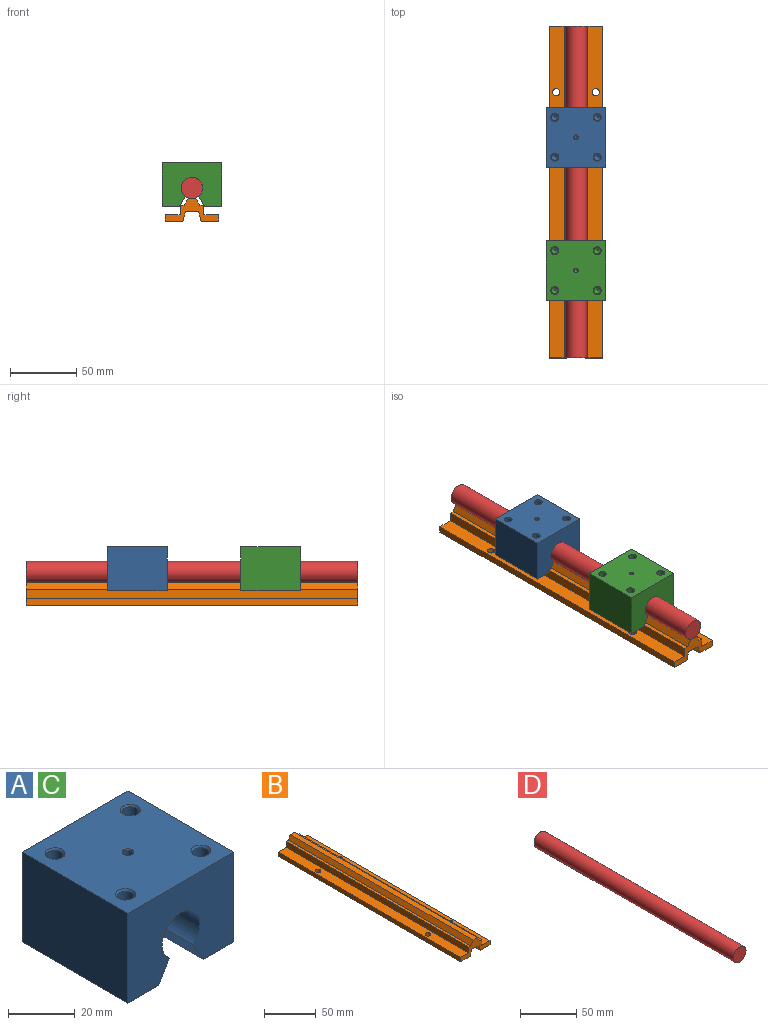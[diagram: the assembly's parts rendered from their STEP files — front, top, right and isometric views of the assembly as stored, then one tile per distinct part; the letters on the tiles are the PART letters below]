
ASSEMBLY  parts=4 mates=2
PART A: 25 faces, bbox 45x45x33 mm
  f0: plane 45x7.77mm, normal (0.87,0,-0.5), area 403.6mm2, adj f1,f7,f8,f9
  f1: cylinder r=8mm len=45mm, axis (0,1,0), area 1774.1mm2, adj f0,f2,f8,f9
  f2: plane 45x7.77mm, normal (-0.87,0,-0.5), area 403.6mm2, adj f1,f3,f8,f9
  f3: plane 45x13mm, normal (0,0,-1), area 585mm2, adj f2,f4,f8,f9
  f4: plane 45x33mm, normal (1,0,0), area 1485mm2, adj f3,f5,f8,f9
  f5: plane 45x45mm, normal (0,0,1), area 1902.3mm2, adj f4,f6,f8,f9,f12,f15,f18,f21
  f6: plane 45x33mm, normal (-1,0,0), area 1485mm2, adj f5,f7,f8,f9
  f7: plane 45x13mm, normal (0,0,-1), area 585mm2, adj f0,f6,f8,f9
  f8: plane 45x33mm, normal (0,-1,0), area 1183.3mm2, adj f0,f1,f2,f3,f4,f5,f6,f7
  f9: plane 45x33mm, normal (0,1,0), area 1183.3mm2, adj f0,f1,f2,f3,f4,f5,f6,f7
  f10: cone r=0mm half-angle=59deg, axis (0,0,1), area 22.9mm2, adj f11
  f11: cylinder r=2.5mm len=11.4mm, axis (0,0,1), area 179.1mm2, adj f10,f12
  f12: cone r=2.5mm half-angle=40deg, axis (0,0,1), area 13.4mm2, adj f5,f11
  f13: cone r=0mm half-angle=59deg, axis (0,0,1), area 22.9mm2, adj f14
  f14: cylinder r=2.5mm len=11.4mm, axis (0,0,1), area 179.1mm2, adj f13,f15
  f15: cone r=2.5mm half-angle=40deg, axis (0,0,1), area 13.4mm2, adj f5,f14
  f16: cone r=0mm half-angle=59deg, axis (0,0,1), area 22.9mm2, adj f17
  f17: cylinder r=2.5mm len=11.4mm, axis (0,0,1), area 179.1mm2, adj f16,f18
  f18: cone r=2.5mm half-angle=40deg, axis (0,0,1), area 13.4mm2, adj f5,f17
  f19: cone r=0mm half-angle=59deg, axis (0,0,1), area 22.9mm2, adj f20
  f20: cylinder r=2.5mm len=11.4mm, axis (0,0,1), area 179.1mm2, adj f19,f21
  f21: cone r=2.5mm half-angle=40deg, axis (0,0,1), area 13.4mm2, adj f5,f20
  f22: cone r=0mm half-angle=59deg, axis (0,0,1), area 8.2mm2, adj f23
  f23: cylinder r=1.5mm len=4.7mm, axis (0,0,1), area 44.3mm2, adj f22,f24
  f24: cone r=1.5mm half-angle=40deg, axis (0,0,1), area 4mm2, adj f5,f23
PART B: 22 faces, bbox 40x250x17 mm
  f0: plane 250x5mm, normal (-1,0,0), area 1250mm2, adj f1,f15,f16,f17
  f1: plane 250x13mm, normal (0,0,-1), area 3202.5mm2, adj f0,f2,f16,f17,f18,f19
  f2: plane 250x7.01mm, normal (0.96,0,-0.27), area 1822.5mm2, adj f1,f3,f16,f17
  f3: plane 250x10mm, normal (0,0,-1), area 2500mm2, adj f2,f4,f16,f17
  f4: plane 250x7.01mm, normal (-0.96,0,-0.27), area 1822.5mm2, adj f3,f5,f16,f17
  f5: plane 250x13mm, normal (0,0,-1), area 3202.5mm2, adj f4,f6,f16,f17,f20,f21
  f6: plane 250x5mm, normal (1,0,0), area 1250mm2, adj f5,f7,f16,f17
  f7: plane 250x11mm, normal (0,0,1), area 2702.5mm2, adj f6,f8,f16,f17,f20,f21
  f8: plane 250x7mm, normal (1,0,0), area 1750mm2, adj f7,f9,f16,f17
  f9: plane 250x3mm, normal (0,0,1), area 750mm2, adj f8,f10,f16,f17
  f10: plane 250x5mm, normal (0.86,0,0.51), area 1457.7mm2, adj f9,f11,f16,f17
  f11: plane 250x6mm, normal (0,0,1), area 1500mm2, adj f10,f12,f16,f17
  f12: plane 250x5mm, normal (-0.86,0,0.51), area 1457.7mm2, adj f11,f13,f16,f17
  f13: plane 250x3mm, normal (0,0,1), area 750mm2, adj f12,f14,f16,f17
  f14: plane 250x7mm, normal (-1,0,0), area 1750mm2, adj f13,f15,f16,f17
  f15: plane 250x11mm, normal (0,0,1), area 2702.5mm2, adj f0,f14,f16,f17,f18,f19
  f16: plane 40x17mm, normal (0,1,0), area 286.9mm2, adj f0,f1,f2,f3,f4,f5,f6,f7
  f17: plane 40x17mm, normal (0,-1,0), area 286.9mm2, adj f0,f1,f2,f3,f4,f5,f6,f7
  f18: cylinder r=2.75mm len=5.5mm, axis (0,0,1), area 86.4mm2, adj f1,f15
  f19: cylinder r=2.75mm len=5.5mm, axis (0,0,1), area 86.4mm2, adj f1,f15
  f20: cylinder r=2.75mm len=5.5mm, axis (0,0,1), area 86.4mm2, adj f5,f7
  f21: cylinder r=2.75mm len=5.5mm, axis (0,0,1), area 86.4mm2, adj f5,f7
PART C: same geometry as A
PART D: 3 faces, bbox 16x250x16 mm
  f0: cylinder r=8mm len=250mm, axis (0,-1,0), area 12566.4mm2, adj f1,f2
  f1: plane 16x16mm, normal (0,1,0), area 201.1mm2, adj f0
  f2: plane 16x16mm, normal (0,-1,0), area 201.1mm2, adj f0
PLACE A t=(0,188.74,11)mm
PLACE B at identity fixed
PLACE C t=(0,88.25,11)mm
PLACE D at identity fixed
MATE slider A.f1 <-> D.f0  axis (0,1,0) through (0,188.74,25)mm
MATE slider C.f1 <-> D.f0  axis (0,1,0) through (0,65.75,25)mm
